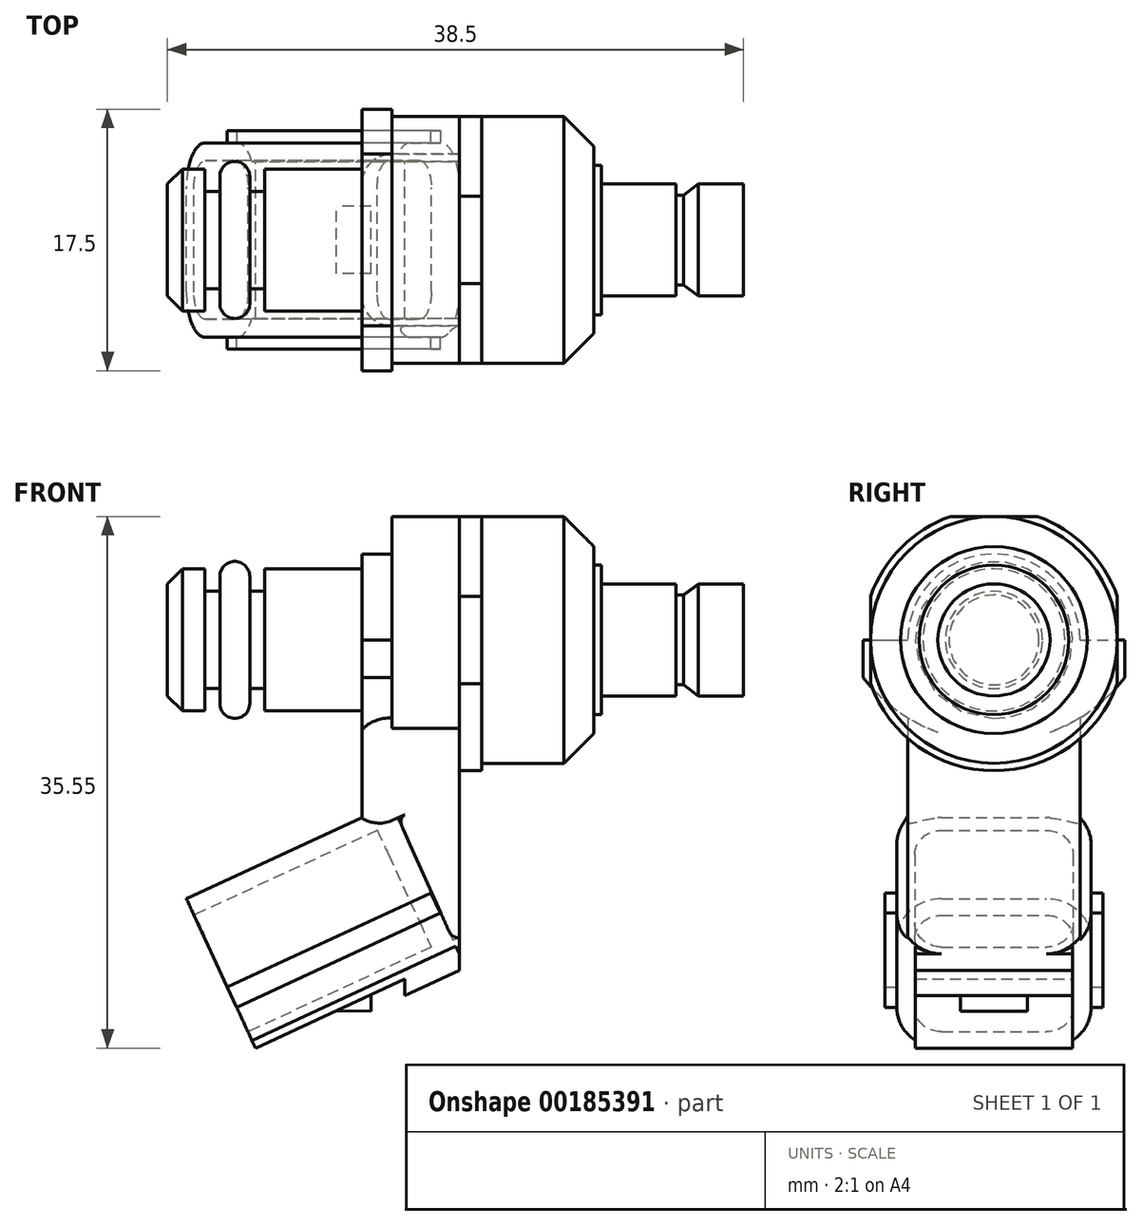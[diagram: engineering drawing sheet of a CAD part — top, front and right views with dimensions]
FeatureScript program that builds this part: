
annotation { "Feature Type Name" : "Feature", "Feature Type Description" : "" }
export const myFeature = defineFeature(function(context is Context, id is Id, definition is map)
    precondition{}
    {
        {
            var Q0;
            Q0=qCreatedBy(makeId("Front.planeOp"),FACE);
            var sketch = newSketch(context, id + "F0", { "sketchPlane" : qUnion([Q0])});
            skLineSegment(sketch, "E0", {"start": v(0, 0) * mm, "end": v(19, 0) * mm});
            skLineSegment(sketch, "E1", {"start": v(19, 0) * mm, "end": v(19, 3.75) * mm});
            skLineSegment(sketch, "E2", {"start": v(19, 3.75) * mm, "end": v(16, 3.75) * mm});
            skLineSegment(sketch, "E3", {"start": v(15, 3) * mm, "end": v(16, 3.75) * mm});
            skLineSegment(sketch, "E4", {"start": v(14.5, 3) * mm, "end": v(15, 3) * mm});
            skLineSegment(sketch, "E5", {"start": v(14.5, 3.75) * mm, "end": v(9.5, 3.75) * mm});
            skLineSegment(sketch, "E6", {"start": v(14.5, 3.75) * mm, "end": v(14.5, 3) * mm});
            skLineSegment(sketch, "E7", {"start": v(9.5, 3.75) * mm, "end": v(9.5, 5) * mm});
            skLineSegment(sketch, "E8", {"start": v(9.5, 5) * mm, "end": v(9, 5) * mm});
            skLineSegment(sketch, "E9", {"start": v(9, 5) * mm, "end": v(9, 8.25) * mm});
            skLineSegment(sketch, "E10", {"start": v(1.5, 8.25) * mm, "end": v(9, 8.25) * mm});
            skLineSegment(sketch, "E11", {"start": v(1.5, 8.25) * mm, "end": v(1.5, 8.75) * mm});
            skLineSegment(sketch, "E12", {"start": v(0, 8.75) * mm, "end": v(1.5, 8.75) * mm});
            skLineSegment(sketch, "E13", {"start": v(9.5, 3.75) * mm, "end": v(9.5, 0) * mm});
            skLineSegment(sketch, "E14", {"start": v(0, 8.75) * mm, "end": v(0, 0) * mm});
            skLineSegment(sketch, "E15", {"start": v(0, 8.25) * mm, "end": v(-4.5, 8.25) * mm});
            skLineSegment(sketch, "E16", {"start": v(-4.5, 8.25) * mm, "end": v(-4.5, 5.75) * mm});
            skLineSegment(sketch, "E17", {"start": v(-4.5, 5.75) * mm, "end": v(-6.5, 5.75) * mm});
            skLineSegment(sketch, "E18", {"start": v(-6.5, 5.75) * mm, "end": v(-6.5, 4.75) * mm});
            skLineSegment(sketch, "E19", {"start": v(-6.5, 4.75) * mm, "end": v(-13, 4.75) * mm});
            skLineSegment(sketch, "E20", {"start": v(-13, 4.75) * mm, "end": v(-13, 3.25) * mm});
            skLineSegment(sketch, "E21", {"start": v(-19.5, 0) * mm, "end": v(-19.5, 4.75) * mm});
            skLineSegment(sketch, "E22", {"start": v(-19.5, 4.75) * mm, "end": v(-17, 4.75) * mm});
            skLineSegment(sketch, "E23", {"start": v(-17, 4.75) * mm, "end": v(-17, 3.25) * mm});
            skLineSegment(sketch, "E24", {"start": v(-17, 3.25) * mm, "end": v(-16, 3.25) * mm});
            skLineSegment(sketch, "E25", {"start": v(-16, 3.25) * mm, "end": v(-16, 5.25) * mm});
            skLineSegment(sketch, "E26", {"start": v(-16, 5.25) * mm, "end": v(-14, 5.25) * mm});
            skLineSegment(sketch, "E27", {"start": v(-14, 5.25) * mm, "end": v(-14, 3.25) * mm});
            skLineSegment(sketch, "E28", {"start": v(-14, 3.25) * mm, "end": v(-13, 3.25) * mm});
            skLineSegment(sketch, "E29", {"start": v(-14, 3.25) * mm, "end": v(-14, 0) * mm});
            skLineSegment(sketch, "E30", {"start": v(-16, 3.25) * mm, "end": v(-16, 0) * mm});
            skLineSegment(sketch, "E31", {"start": v(-19.5, 0) * mm, "end": v(0, 0) * mm});
            skLineSegment(sketch, "E32", {"start": v(-16, 3.25) * mm, "end": v(-14, 3.25) * mm});
            skSolve(sketch);
        }
        {
            var Q0;
            {var subQ0=sQuery(id+"F0.wireOp",EDGE,"E1");Q0=makeQuery(id+"F0.imprint","IMPRINT",FACE,{"disambiguationData":[TD([[makeQuery(id+"F0.imprint","IMPRINT",EDGE,{"derivedFrom":subQ0}),1.0]])]});}
            var Q1;
            Q1=makeQuery(id+"F0.imprint","IMPRINT",FACE,{"disambiguationData":[TD([[makeQuery(id+"F0.imprint","IMPRINT",EDGE,{"derivedFrom":sQuery(id+"F0.wireOp",EDGE,"E7")}),1.0]])]});
            var Q2;
            {var subQ0=sQuery(id+"F0.wireOp",EDGE,"E15");Q2=makeQuery(id+"F0.imprint","IMPRINT",FACE,{"disambiguationData":[TD([[makeQuery(id+"F0.imprint","IMPRINT",EDGE,{"derivedFrom":subQ0}),1.0]])]});}
            var Q3;
            {var subQ0=sQuery(id+"F0.wireOp",EDGE,"E29");Q3=makeQuery(id+"F0.imprint","IMPRINT",FACE,{"disambiguationData":[TD([[makeQuery(id+"F0.imprint","IMPRINT",EDGE,{"derivedFrom":subQ0}),-1.0]])]});}
            var Q4;
            Q4=makeQuery(id+"F0.imprint","IMPRINT",FACE,{"disambiguationData":[TD([[makeQuery(id+"F0.imprint","IMPRINT",EDGE,{"derivedFrom":sQuery(id+"F0.wireOp",EDGE,"E25")}),-1.0]])]});
            var Q5;
            {var subQ0=sQuery(id+"F0.wireOp",EDGE,"E21");Q5=makeQuery(id+"F0.imprint","IMPRINT",FACE,{"disambiguationData":[TD([[makeQuery(id+"F0.imprint","IMPRINT",EDGE,{"derivedFrom":subQ0}),-1.0]])]});}
            var Q6;
            Q6=sQuery(id+"F0.wireOp",EDGE,"E0");
            revolve(context, id + "F1", {"entities" : qUnion([Q0, Q1, Q2, Q3, Q4, Q5]), "axis" : qUnion([Q6]), "revolveType" : RevolveType.FULL});
        }
        {
            var Q0;
            Q0=qCreatedBy(makeId("Front.planeOp"),FACE);
            var sketch = newSketch(context, id + "F2", { "sketchPlane" : qUnion([Q0])});
            skLineSegment(sketch, "E33", {"start": v(0, 0) * mm, "end": v(-4.5, 0) * mm});
            skLineSegment(sketch, "E34", {"start": v(-4.5, 0) * mm, "end": v(-4.5, -10.96) * mm});
            skLineSegment(sketch, "E35", {"start": v(0, 0) * mm, "end": v(0, 4.75) * mm});
            skLineSegment(sketch, "E36", {"start": v(0, 4.75) * mm, "end": v(0, -21) * mm});
            skLineSegment(sketch, "E37", {"start": v(0, 0) * mm, "end": v(0, -21) * mm});
            skLineSegment(sketch, "E38", {"start": v(0, -21) * mm, "end": v(-13.61, -27.3) * mm});
            skLineSegment(sketch, "E39.0", {"start": v(-4.5, -10.96) * mm, "end": v(-18.23, -17.32) * mm});
            skLineSegment(sketch, "E40", {"start": v(-18.23, -17.32) * mm, "end": v(-13.61, -27.3) * mm});
            skLineSegment(sketch, "E41", {"start": v(-4.5, -10.96) * mm, "end": v(0, -21) * mm});
            skLineSegment(sketch, "E42.0", {"start": v(0.42, -21.9) * mm, "end": v(-3.63, -23.78) * mm});
            skLineSegment(sketch, "E43", {"start": v(0, -21) * mm, "end": v(0, -22.1) * mm});
            skLineSegment(sketch, "E44", {"start": v(0, -22.1) * mm, "end": v(-3.63, -23.78) * mm});
            skLineSegment(sketch, "E45", {"start": v(-3.63, -23.78) * mm, "end": v(-3.63, -22.68) * mm});
            skLineSegment(sketch, "E46", {"start": v(-5.9, -24.83) * mm, "end": v(-5.9, -23.73) * mm});
            skLineSegment(sketch, "E47", {"start": v(-5.9, -23.73) * mm, "end": v(-5.77, -23.7) * mm});
            skLineSegment(sketch, "E48", {"start": v(-8.21, -24.8) * mm, "end": v(-5.9, -24.83) * mm});
            skSolve(sketch);
        }
        {
            var Q0;
            Q0=makeQuery(id+"F2.imprint","IMPRINT",FACE,{"disambiguationData":[TD([[makeQuery(id+"F2.imprint","IMPRINT",EDGE,{"derivedFrom":sQuery(id+"F2.wireOp",EDGE,"E33")}),1.0]])]});
            extrude(context, id + "F3", {"entities" : qUnion([Q0]), "operationType" : NewBodyOperationType.ADD, "endBound" : BoundingType.SYMMETRIC, "depth" : 11.5 * mm});
        }
        {
            var Q0;
            Q0=makeQuery(id+"F2.imprint","IMPRINT",FACE,{"disambiguationData":[TD([[makeQuery(id+"F2.imprint","IMPRINT",EDGE,{"derivedFrom":sQuery(id+"F2.wireOp",EDGE,"E38")}),-1.0]])]});
            extrude(context, id + "F4", {"entities" : qUnion([Q0]), "operationType" : NewBodyOperationType.ADD, "endBound" : BoundingType.SYMMETRIC, "depth" : 13 * mm});
        }
        {
            var Q0;
            Q0=makeQuery(id+"F1.opRevolve","SWEPT_EDGE",EDGE,{"disambiguationData":[OSD([sQuery(id+"F0.wireOp",EDGE,"E21"),sQuery(id+"F0.wireOp",EDGE,"E22")])]});
            chamfer(context, id + "F5", {"entities" : qUnion([Q0]), "width" : 1 * mm, "tangentPropagation" : true});
        }
        {
            var Q0;
            Q0=makeQuery(id+"F1.opRevolve","SWEPT_EDGE",EDGE,{"disambiguationData":[OSD([sQuery(id+"F0.wireOp",EDGE,"E26"),sQuery(id+"F0.wireOp",EDGE,"E27")])]});
            var Q1;
            Q1=makeQuery(id+"F1.opRevolve","SWEPT_EDGE",EDGE,{"disambiguationData":[OSD([sQuery(id+"F0.wireOp",EDGE,"E25"),sQuery(id+"F0.wireOp",EDGE,"E26")])]});
            fillet(context, id + "F6", {"entities" : qUnion([Q0, Q1]), "radius" : 1 * mm, "tangentPropagation" : true, "allowEdgeOverflow" : false});
        }
        {
            var Q0;
            Q0=makeQuery(id+"F1.opRevolve","SWEPT_EDGE",EDGE,{"disambiguationData":[OSD([sQuery(id+"F0.wireOp",EDGE,"E9"),sQuery(id+"F0.wireOp",EDGE,"E10")])]});
            chamfer(context, id + "F7", {"entities" : qUnion([Q0]), "width" : 2 * mm, "tangentPropagation" : true});
        }
        {
            var Q0;
            Q0=makeQuery(id+"F3.boolean.opBoolean","MERGE",FACE,{"derivedFrom":[makeQuery(id+"F1.opRevolve","SWEPT_FACE",FACE,{"disambiguationData":[OSD([sQuery(id+"F0.wireOp",EDGE,"E16")])]}),makeQuery(id+"F3.opExtrude","SWEPT_FACE",FACE,{"disambiguationData":[OSD([sQuery(id+"F2.wireOp",EDGE,"E34")])]})]});
            var sketch = newSketch(context, id + "F8", { "sketchPlane" : qUnion([Q0])});
            skLineSegment(sketch, "E49", {"start": v(0, 0) * mm, "end": v(-8.75, 0) * mm});
            skLineSegment(sketch, "E50", {"start": v(-8.75, 0) * mm, "end": v(-8.75, -2.5) * mm});
            skLineSegment(sketch, "E51.MirrorCS", {"start": v(0, 0) * mm, "end": v(8.75, 0) * mm});
            skLineSegment(sketch, "E52.MirrorCS", {"start": v(8.75, 0) * mm, "end": v(8.75, -2.5) * mm});
            skArc(sketch, "E53", {"start": v(-8.75, -2.5) * mm, "mid": v(-7.37, -4) * mm, "end": v(-5.75, -5.2) * mm});
            skArc(sketch, "E54.MirrorCS", {"start": v(8.75, -2.5) * mm, "mid": v(7.37, -4) * mm, "end": v(5.75, -5.2) * mm});
            skLineSegment(sketch, "E55", {"start": v(-5.75, -5.2) * mm, "end": v(-5.75, -14.5) * mm});
            skLineSegment(sketch, "E56.MirrorCS", {"start": v(5.75, -5.2) * mm, "end": v(5.75, -14.5) * mm});
            skLineSegment(sketch, "E57", {"start": v(5.75, -14.5) * mm, "end": v(-5.75, -14.5) * mm});
            skPoint(sketch, "E58.orphan", {"position": v(0, -6.86) * mm});
            skSolve(sketch);
        }
        {
            var Q0;
            Q0 = qSketchRegion(id + "F8", true);
            extrude(context, id + "F9", {"entities" : qUnion([Q0]), "operationType" : NewBodyOperationType.ADD, "depth" : 2 * mm});
        }
        {
            var Q0;
            Q0=makeQuery(id+"F4.opExtrude","CAP_EDGE",EDGE,{"disambiguationData":[OSD([sQuery(id+"F2.wireOp",EDGE,"E39.0")])],"isStart":true});
            var Q1;
            Q1=makeQuery(id+"F4.opExtrude","CAP_EDGE",EDGE,{"disambiguationData":[OSD([sQuery(id+"F2.wireOp",EDGE,"E39.0")])],"isStart":false});
            var Q2;
            Q2=makeQuery(id+"F4.opExtrude","CAP_EDGE",EDGE,{"disambiguationData":[OSD([sQuery(id+"F2.wireOp",EDGE,"E38")])],"isStart":true});
            var Q3;
            Q3=makeQuery(id+"F4.opExtrude","CAP_EDGE",EDGE,{"disambiguationData":[OSD([sQuery(id+"F2.wireOp",EDGE,"E38")])],"isStart":false});
            fillet(context, id + "F10", {"entities" : qUnion([Q0, Q1, Q2, Q3]), "radius" : 3 * mm, "tangentPropagation" : true, "allowEdgeOverflow" : false});
        }
        {
            var Q0;
            Q0=makeQuery(id+"F4.opExtrude","SWEPT_FACE",FACE,{"disambiguationData":[OSD([sQuery(id+"F2.wireOp",EDGE,"E40")])]});
            var sketch = newSketch(context, id + "F11", { "sketchPlane" : qUnion([Q0])});
            skLineSegment(sketch, "E59.0", {"start": v(5.3, -11.06) * mm, "end": v(5.3, -16.06) * mm});
            skLineSegment(sketch, "E59.1", {"start": v(-5.3, -11.06) * mm, "end": v(-5.3, -16.06) * mm});
            skArc(sketch, "E59.2", {"start": v(-3.5, -9.26) * mm, "mid": v(-4.77, -9.78) * mm, "end": v(-5.3, -11.06) * mm});
            skLineSegment(sketch, "E59.3", {"start": v(3.5, -17.86) * mm, "end": v(-3.5, -17.86) * mm});
            skLineSegment(sketch, "E59.4", {"start": v(3.5, -9.26) * mm, "end": v(-3.5, -9.26) * mm});
            skArc(sketch, "E59.5", {"start": v(5.3, -11.06) * mm, "mid": v(4.77, -9.78) * mm, "end": v(3.5, -9.26) * mm});
            skPoint(sketch, "E60.visualSharp", {"position": v(-5.3, -17.86) * mm});
            skArc(sketch, "E60.filletArc", {"start": v(-5.3, -16.06) * mm, "mid": v(-4.77, -17.33) * mm, "end": v(-3.5, -17.86) * mm});
            skPoint(sketch, "E61.visualSharp", {"position": v(5.3, -17.86) * mm});
            skArc(sketch, "E61.filletArc", {"start": v(3.5, -17.86) * mm, "mid": v(4.77, -17.33) * mm, "end": v(5.3, -16.06) * mm});
            skSolve(sketch);
        }
        {
            var Q0;
            Q0=makeQuery(id+"F11.imprint","IMPRINT",FACE,{"disambiguationData":[TD([[makeQuery(id+"F11.imprint","IMPRINT",EDGE,{"derivedFrom":sQuery(id+"F11.wireOp",EDGE,"E59.0")}),-1.0]])]});
            extrude(context, id + "F12", {"entities" : qUnion([Q0]), "operationType" : NewBodyOperationType.REMOVE, "oppositeDirection" : true, "depth" : 13.5 * mm});
        }
        {
            var Q0;
            Q0=makeQuery(id+"F4.opExtrude","SWEPT_FACE",FACE,{"disambiguationData":[OSD([sQuery(id+"F2.wireOp",EDGE,"E40")])]});
            var sketch = newSketch(context, id + "F13", { "sketchPlane" : qUnion([Q0])});
            skLineSegment(sketch, "E62.0", {"start": v(7.3, -14.56) * mm, "end": v(7.3, -16.06) * mm});
            skLineSegment(sketch, "E63", {"start": v(7.3, -16.06) * mm, "end": v(6.5, -16.06) * mm});
            skLineSegment(sketch, "E64", {"start": v(6.5, -14.56) * mm, "end": v(7.3, -14.56) * mm});
            skLineSegment(sketch, "E65.MirrorCS", {"start": v(-7.3, -14.56) * mm, "end": v(-7.3, -16.06) * mm});
            skLineSegment(sketch, "E66.MirrorCS", {"start": v(-7.3, -16.06) * mm, "end": v(-6.5, -16.06) * mm});
            skLineSegment(sketch, "E67.MirrorCS", {"start": v(-6.5, -14.56) * mm, "end": v(-7.3, -14.56) * mm});
            skLineSegment(sketch, "E68", {"start": v(0, -19.06) * mm, "end": v(5.25, -19.06) * mm});
            skLineSegment(sketch, "E69.MirrorCS", {"start": v(-5.25, -19.06) * mm, "end": v(-5.25, -18.04) * mm});
            skLineSegment(sketch, "E70.MirrorCS", {"start": v(0, -19.06) * mm, "end": v(-5.25, -19.06) * mm});
            skLineSegment(sketch, "E71", {"start": v(-6.52, -16.08) * mm, "end": v(-6.12, -16.08) * mm});
            skLineSegment(sketch, "E72", {"start": v(-6.12, -16.08) * mm, "end": v(-6.12, -14.5) * mm});
            skLineSegment(sketch, "E73", {"start": v(-6.12, -14.5) * mm, "end": v(-6.5, -14.56) * mm});
            skLineSegment(sketch, "E74", {"start": v(6.05, -16.06) * mm, "end": v(6.05, -14.56) * mm});
            skLineSegment(sketch, "E75", {"start": v(6.5, -14.56) * mm, "end": v(6.05, -14.56) * mm});
            skLineSegment(sketch, "E76", {"start": v(6.5, -16.06) * mm, "end": v(6.05, -16.06) * mm});
            skLineSegment(sketch, "E77", {"start": v(-5.25, -18.04) * mm, "end": v(-3.5, -19.06) * mm});
            skLineSegment(sketch, "E78", {"start": v(5.25, -19.06) * mm, "end": v(5.25, -18.5) * mm});
            skLineSegment(sketch, "E79", {"start": v(5.25, -18.5) * mm, "end": v(3.5, -19.06) * mm});
            skSolve(sketch);
        }
        {
            var Q0;
            {var subQ7=sQuery(id+"F13.wireOp",EDGE,"E72");Q0=makeQuery(id+"F13.imprint","IMPRINT",FACE,{"disambiguationData":[TD([[makeQuery(id+"F13.imprint","IMPRINT",EDGE,{"derivedFrom":subQ7}),1.0]])]});}
            var Q1;
            Q1=makeQuery(id+"F13.imprint","IMPRINT",FACE,{"disambiguationData":[TD([[makeQuery(id+"F13.imprint","IMPRINT",EDGE,{"derivedFrom":sQuery(id+"F13.wireOp",EDGE,"E65.MirrorCS")}),1.0]])]});
            var Q2;
            Q2=makeQuery(id+"F13.imprint","IMPRINT",FACE,{"disambiguationData":[TD([[makeQuery(id+"F13.imprint","IMPRINT",EDGE,{"derivedFrom":sQuery(id+"F13.wireOp",EDGE,"E74")}),-1.0]])]});
            var Q3;
            {var subQ4=sQuery(id+"F13.wireOp",EDGE,"hCakwlDt-KKLH-bCBa-GUGp-bKXBa02o0HDb");Q3=makeQuery(id+"F13.imprint","IMPRINT",FACE,{"disambiguationData":[TD([[makeQuery(id+"F13.imprint","IMPRINT",EDGE,{"derivedFrom":subQ4}),1.0]])]});}
            var Q4;
            {var subQ0=sQuery(id+"F13.wireOp",EDGE,"1xjOxcos-U0MI-UvO1-PXT8-Ll3OemfaZc8I");Q4=makeQuery(id+"F13.imprint","IMPRINT",FACE,{"disambiguationData":[TD([[makeQuery(id+"F13.imprint","IMPRINT",EDGE,{"derivedFrom":subQ0}),1.0]])]});}
            var Q5;
            {var subQ0=sQuery(id+"F13.wireOp",EDGE,"E69.MirrorCS");Q5=makeQuery(id+"F13.imprint","IMPRINT",FACE,{"disambiguationData":[TD([[makeQuery(id+"F13.imprint","IMPRINT",EDGE,{"derivedFrom":subQ0}),-1.0]])]});}
            var Q6;
            {var subQ0=sQuery(id+"F13.wireOp",EDGE,"E77");Q6=makeQuery(id+"F13.imprint","IMPRINT",FACE,{"disambiguationData":[TD([[makeQuery(id+"F13.imprint","IMPRINT",EDGE,{"derivedFrom":subQ0}),-1.0]])]});}
            var Q7;
            Q7=makeQuery(id+"F13.imprint","IMPRINT",FACE,{"disambiguationData":[TD([[makeQuery(id+"F13.imprint","IMPRINT",EDGE,{"derivedFrom":sQuery(id+"F13.wireOp",EDGE,"E62.0")}),-1.0]])]});
            var Q8;
            {var subQ4=sQuery(id+"F13.wireOp",EDGE,"E78");Q8=makeQuery(id+"F13.imprint","IMPRINT",FACE,{"disambiguationData":[TD([[makeQuery(id+"F13.imprint","IMPRINT",EDGE,{"derivedFrom":subQ4}),1.0]])]});}
            extrude(context, id + "F14", {"entities" : qUnion([Q0, Q1, Q2, Q3, Q4, Q5, Q6, Q7, Q8]), "operationType" : NewBodyOperationType.ADD, "oppositeDirection" : true, "depth" : 15 * mm});
        }
        {
            var Q0;
            {var subQ0=sQuery(id+"F2.wireOp",EDGE,"E43");Q0=makeQuery(id+"F2.imprint","IMPRINT",FACE,{"disambiguationData":[TD([[makeQuery(id+"F2.imprint","IMPRINT",EDGE,{"derivedFrom":subQ0}),-1.0]])]});}
            extrude(context, id + "F15", {"entities" : qUnion([Q0]), "operationType" : NewBodyOperationType.ADD, "endBound" : BoundingType.SYMMETRIC, "depth" : 10.5 * mm});
        }
        {
            var Q0;
            Q0=makeQuery(id+"F1.opRevolve","SWEPT_FACE",FACE,{"disambiguationData":[OSD([sQuery(id+"F0.wireOp",EDGE,"E11")])]});
            var sketch = newSketch(context, id + "F16", { "sketchPlane" : qUnion([Q0])});
            skLineSegment(sketch, "E80", {"start": v(0, 8.25) * mm, "end": v(2.92, 8.25) * mm});
            skArc(sketch, "E81", {"start": v(-8.25, 2.92) * mm, "mid": v(-8.75, 0) * mm, "end": v(-8.25, -2.92) * mm});
            skLineSegment(sketch, "E82", {"start": v(8.25, 0) * mm, "end": v(8.25, 2.92) * mm});
            skLineSegment(sketch, "E83", {"start": v(0, 8.25) * mm, "end": v(-2.92, 8.25) * mm});
            skLineSegment(sketch, "E84", {"start": v(8.25, 0) * mm, "end": v(8.25, -2.92) * mm});
            skLineSegment(sketch, "E85", {"start": v(-8.25, 0) * mm, "end": v(-8.25, 2.92) * mm});
            skLineSegment(sketch, "E86", {"start": v(-8.25, 0) * mm, "end": v(-8.25, -2.92) * mm});
            skArc(sketch, "E87.trimOffspring", {"start": v(2.92, 8.25) * mm, "mid": v(0, 8.75) * mm, "end": v(-2.92, 8.25) * mm});
            skArc(sketch, "E88.trimOffspring", {"start": v(8.25, -2.92) * mm, "mid": v(8.75, 0) * mm, "end": v(8.25, 2.92) * mm});
            skSolve(sketch);
        }
        {
            var Q0;
            Q0=makeQuery(id+"F16.imprint","IMPRINT",FACE,{"disambiguationData":[TD([[makeQuery(id+"F16.imprint","IMPRINT",EDGE,{"derivedFrom":sQuery(id+"F16.wireOp",EDGE,"E80")}),1.0]])]});
            var Q1;
            Q1=makeQuery(id+"F16.imprint","IMPRINT",FACE,{"disambiguationData":[TD([[makeQuery(id+"F16.imprint","IMPRINT",EDGE,{"derivedFrom":sQuery(id+"F16.wireOp",EDGE,"E81")}),-1.0]])]});
            var Q2;
            Q2=makeQuery(id+"F16.imprint","IMPRINT",FACE,{"disambiguationData":[TD([[makeQuery(id+"F16.imprint","IMPRINT",EDGE,{"derivedFrom":sQuery(id+"F16.wireOp",EDGE,"E82")}),-1.0]])]});
            extrude(context, id + "F17", {"entities" : qUnion([Q0, Q1, Q2]), "operationType" : NewBodyOperationType.REMOVE, "oppositeDirection" : true, "depth" : 3 * mm});
        }
        {
            var Q0;
            {var subQ0=sQuery(id+"F2.wireOp",EDGE,"E46");Q0=makeQuery(id+"F2.imprint","IMPRINT",FACE,{"disambiguationData":[TD([[makeQuery(id+"F2.imprint","IMPRINT",EDGE,{"derivedFrom":subQ0}),1.0]])]});}
            extrude(context, id + "F18", {"entities" : qUnion([Q0]), "operationType" : NewBodyOperationType.ADD, "endBound" : BoundingType.SYMMETRIC, "depth" : 4.5 * mm});
        }
        {
            var Q0;
            Q0=makeQuery(id+"F9.opExtrude","CAP_EDGE",EDGE,{"disambiguationData":[OSD([sQuery(id+"F8.wireOp",EDGE,"E55")])],"isStart":false});
            var Q1;
            Q1=makeQuery(id+"F9.opExtrude","CAP_EDGE",EDGE,{"disambiguationData":[OSD([sQuery(id+"F8.wireOp",EDGE,"E56.MirrorCS")])],"isStart":false});
            fillet(context, id + "F19", {"entities" : qUnion([Q0, Q1]), "radius" : 2 * mm, "tangentPropagation" : true, "allowEdgeOverflow" : false});
        }
        {
            var Q0;
            Q0=makeQuery(id+"F3.opExtrude","CAP_EDGE",EDGE,{"disambiguationData":[OSD([sQuery(id+"F2.wireOp",EDGE,"E41")])],"isStart":true});
            var Q1;
            Q1=makeQuery(id+"F3.opExtrude","CAP_EDGE",EDGE,{"disambiguationData":[OSD([sQuery(id+"F2.wireOp",EDGE,"E41")])],"isStart":false});
            fillet(context, id + "F20", {"entities" : qUnion([Q0, Q1]), "radius" : 0.5 * mm, "tangentPropagation" : true, "allowEdgeOverflow" : false});
        }
    });
